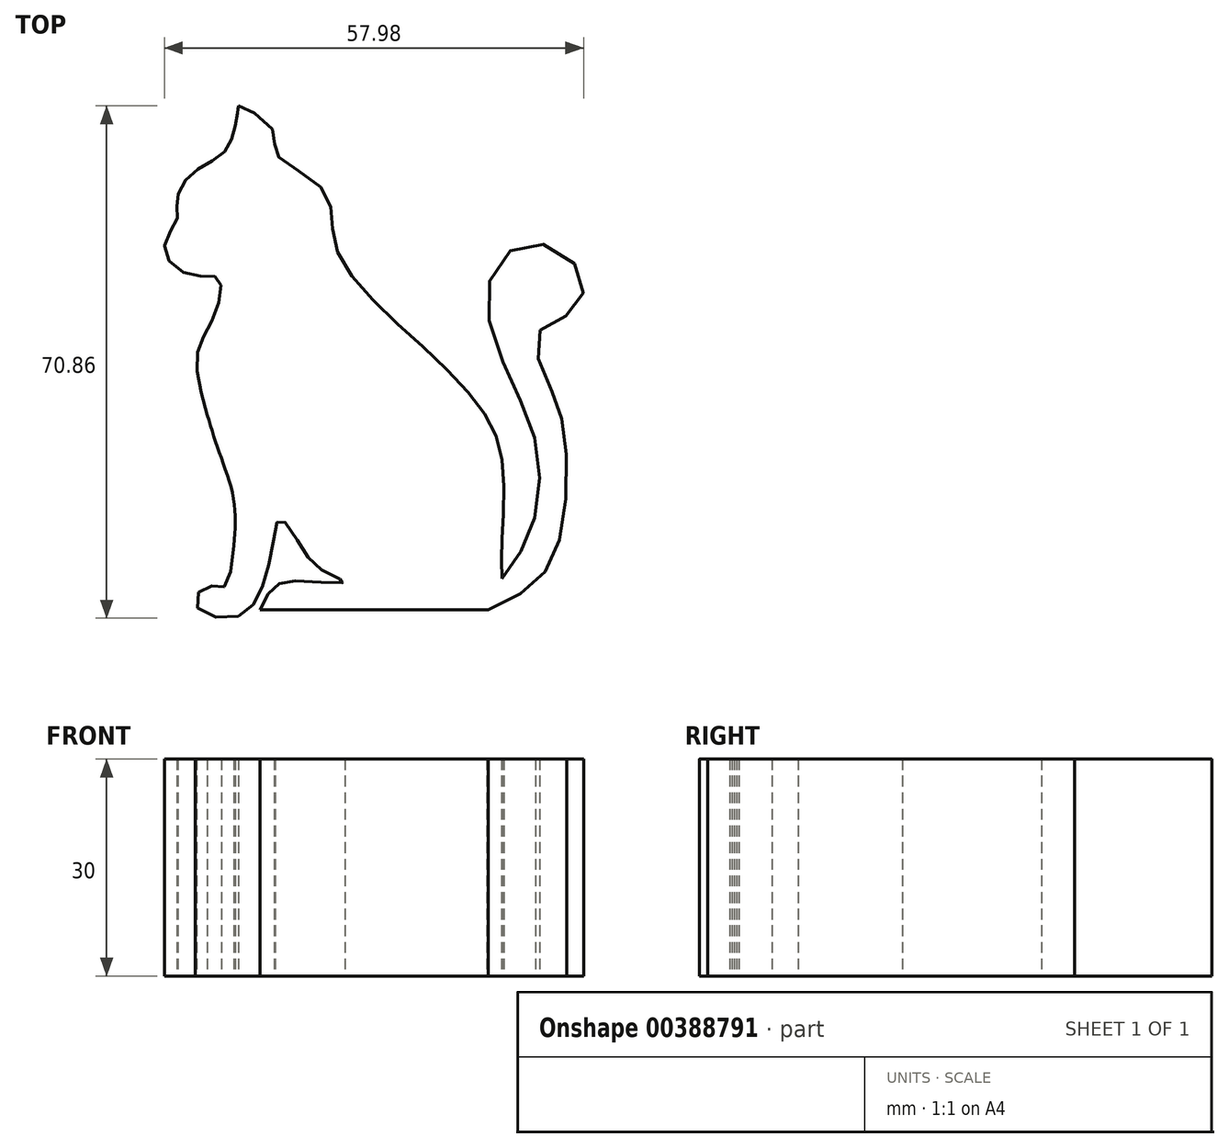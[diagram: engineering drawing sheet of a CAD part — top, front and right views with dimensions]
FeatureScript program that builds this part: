
annotation { "Feature Type Name" : "Feature", "Feature Type Description" : "" }
export const myFeature = defineFeature(function(context is Context, id is Id, definition is map)
    precondition{}
    {
        {
            var Q0;
            Q0=qCreatedBy(makeId("Top.planeOp"),FACE);
            var sketch = newSketch(context, id + "F0", { "sketchPlane" : qUnion([Q0])});
            skFitSpline(sketch, "E0", {"points": [v(-14.72, 24.97) * mm, v(-15.21, 21.89) * mm, v(-16.81, 18.43) * mm, v(-21, 15.72) * mm, v(-23.22, 12.03) * mm, v(-23.22, 9.31) * mm, v(-24.95, 5.25) * mm, v(-21.25, 1.55) * mm, v(-17.43, 1.06) * mm, v(-18.04, -4) * mm, v(-20.39, -9.3) * mm, v(-19.03, -17.8) * mm], "startDerivative": vector(-5.1, -39.95) * mm, "endDerivative": vector(21.04, -74.6) * mm});
            skFitSpline(sketch, "E1", {"points": [v(-19.03, -17.8) * mm, v(-17.26, -23.27) * mm, v(-15.34, -29.63) * mm, v(-15.34, -35.82) * mm], "startDerivative": vector(5.14, -16.68) * mm, "endDerivative": vector(-1.46, -18.5) * mm});
            skFitSpline(sketch, "E2", {"points": [v(-15.34, -35.82) * mm, v(-16.77, -41.6) * mm, v(-19.03, -41.43) * mm, v(-20.6, -44.05) * mm, v(-15.34, -45.79) * mm, v(-11.89, -42.65) * mm, v(-9.97, -35.82) * mm, v(-8.93, -32.2) * mm, v(-6.14, -35.82) * mm, v(-3, -39.34) * mm, v(0, -40.9) * mm, v(-5.79, -40.73) * mm, v(-9.62, -41.43) * mm, v(-11.72, -44.74) * mm], "startDerivative": vector(-8.2, -90.44) * mm, "endDerivative": vector(-25.44, -54.15) * mm});
            skLineSegment(sketch, "E3", {"start": v(-11.72, -44.74) * mm, "end": v(19.83, -44.74) * mm});
            skFitSpline(sketch, "E4", {"points": [v(19.83, -44.74) * mm, v(26.98, -40.39) * mm, v(30.29, -32.02) * mm, v(30.29, -19.65) * mm, v(28.37, -13.9) * mm, v(26.63, -6.57) * mm, v(31.5, -3.44) * mm, v(32.55, 1.97) * mm, v(25.4, 5.97) * mm, v(19.83, 0) * mm, v(22.45, -11.8) * mm, v(26.63, -22.43) * mm, v(25.76, -33.59) * mm, v(21.75, -40.39) * mm], "startDerivative": vector(105.46, 47.48) * mm, "endDerivative": vector(-61.7, -82.89) * mm});
            skFitSpline(sketch, "E5", {"points": [v(21.75, -40.39) * mm, v(21.75, -34.46) * mm, v(21.75, -24) * mm, v(17.91, -15.64) * mm, v(6.76, -4.66) * mm, v(-1.43, 5.97) * mm, v(-2.83, 13.12) * mm, v(-9.62, 18.52) * mm, v(-9.8, 21.31) * mm, v(-14.72, 24.97) * mm, v(-14.84, 23.97) * mm], "startDerivative": vector(-1.57, 60.14) * mm, "endDerivative": vector(8.06, -37.53) * mm});
            skSolve(sketch);
        }
        {
            var Q0;
            {var subQ0=sQuery(id+"F0.wireOp",EDGE,"E1");Q0=makeQuery(id+"F0.imprint","IMPRINT",FACE,{"disambiguationData":[TD([[makeQuery(id+"F0.imprint","IMPRINT",EDGE,{"derivedFrom":subQ0}),1.0]])]});}
            extrude(context, id + "F1", {"entities" : qUnion([Q0]), "depth" : 30 * mm});
        }
    });
